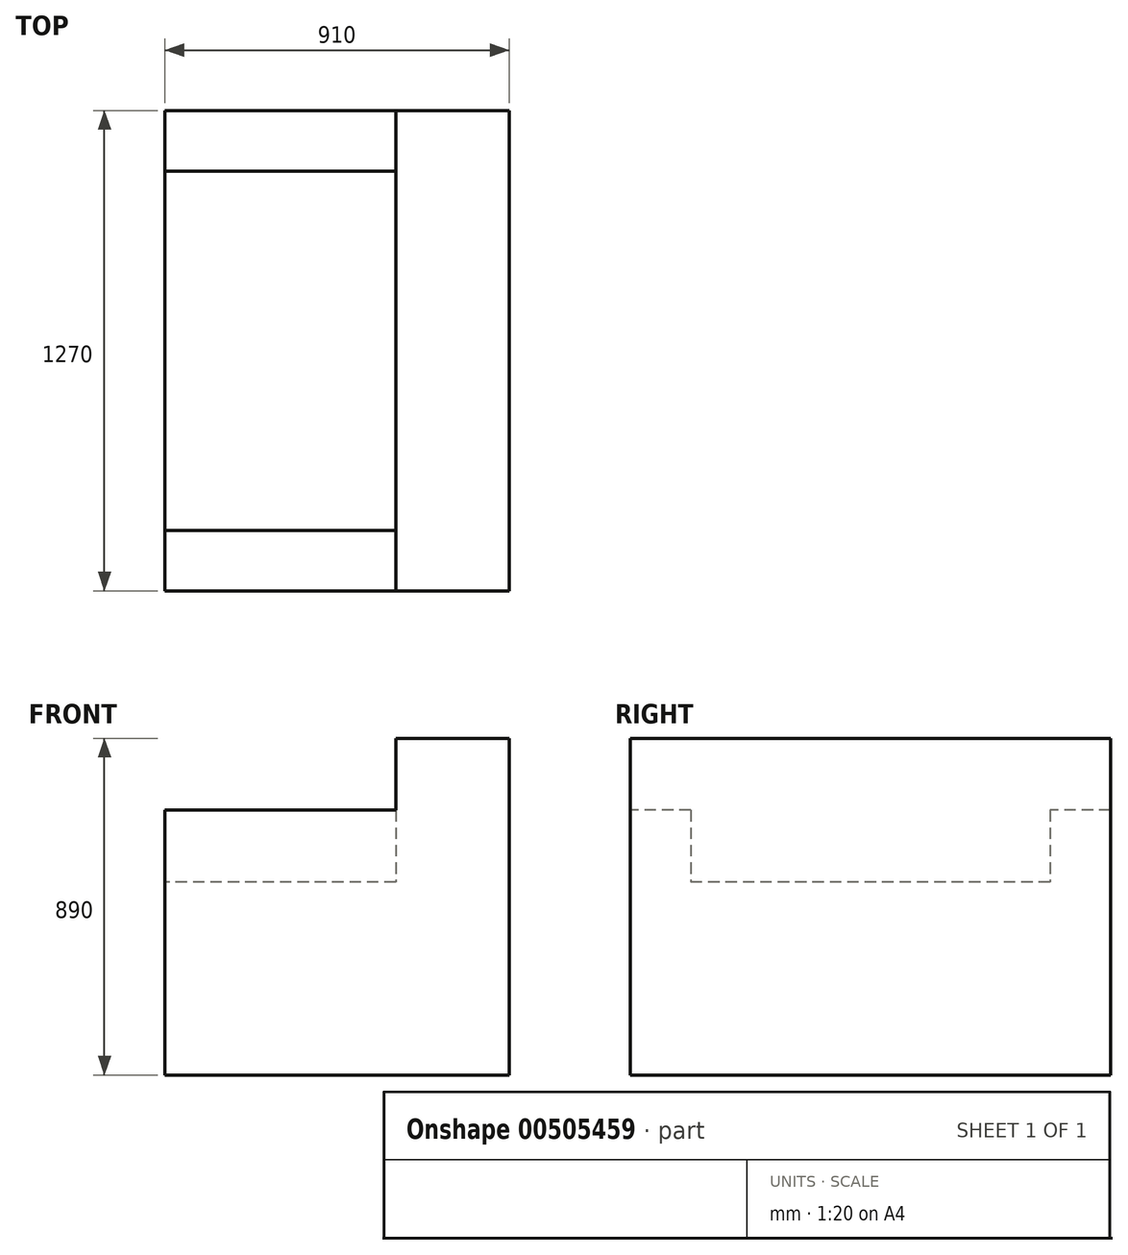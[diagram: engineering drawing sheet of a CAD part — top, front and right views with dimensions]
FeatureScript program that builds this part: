
annotation { "Feature Type Name" : "Feature", "Feature Type Description" : "" }
export const myFeature = defineFeature(function(context is Context, id is Id, definition is map)
    precondition{}
    {
        {
            var Q0;
            Q0=qCreatedBy(makeId("Top.planeOp"),FACE);
            var sketch = newSketch(context, id + "F0", { "sketchPlane" : qUnion([Q0])});
            skLineSegment(sketch, "E0.bottom", {"start": v(465.5, 635) * mm, "end": v(-444.5, 635) * mm});
            skLineSegment(sketch, "E0.top", {"start": v(465.5, -635) * mm, "end": v(-444.5, -635) * mm});
            skLineSegment(sketch, "E0.left", {"start": v(465.5, 635) * mm, "end": v(465.5, -635) * mm});
            skLineSegment(sketch, "E0.right", {"start": v(-444.5, 635) * mm, "end": v(-444.5, -635) * mm});
            skPoint(sketch, "E0.middle", {"position": v(10.5, 0) * mm});
            skSolve(sketch);
        }
        {
            var Q0;
            Q0 = qSketchRegion(id + "F0", true);
            extrude(context, id + "F1", {"entities" : qUnion([Q0]), "depth" : 890 * mm});
        }
        {
            var Q0;
            Q0=makeQuery(id+"F1.opExtrude","SWEPT_FACE",FACE,{"disambiguationData":[OSD([sQuery(id+"F0.wireOp",EDGE,"E0.right")])]});
            var sketch = newSketch(context, id + "F2", { "sketchPlane" : qUnion([Q0])});
            skLineSegment(sketch, "E1.bottom", {"start": v(-475, 890) * mm, "end": v(475, 890) * mm});
            skLineSegment(sketch, "E1.top", {"start": v(-475, 510) * mm, "end": v(475, 510) * mm});
            skLineSegment(sketch, "E1.left", {"start": v(-475, 890) * mm, "end": v(-475, 510) * mm});
            skLineSegment(sketch, "E1.right", {"start": v(475, 890) * mm, "end": v(475, 510) * mm});
            skLineSegment(sketch, "E2", {"start": v(0, 890) * mm, "end": v(0, 510) * mm, "construction": true});
            skSolve(sketch);
        }
        {
            var Q0;
            Q0 = qSketchRegion(id + "F2", true);
            extrude(context, id + "F3", {"entities" : qUnion([Q0]), "operationType" : NewBodyOperationType.REMOVE, "oppositeDirection" : true, "depth" : 610 * mm});
        }
        {
            var Q0;
            Q0=makeQuery(id+"F1.opExtrude","SWEPT_FACE",FACE,{"disambiguationData":[OSD([sQuery(id+"F0.wireOp",EDGE,"E0.right")])]});
            var sketch = newSketch(context, id + "F4", { "sketchPlane" : qUnion([Q0])});
            skLineSegment(sketch, "E3.bottom", {"start": v(-635, 890) * mm, "end": v(-475, 890) * mm});
            skLineSegment(sketch, "E3.top", {"start": v(-635, 700) * mm, "end": v(-475, 700) * mm});
            skLineSegment(sketch, "E3.left", {"start": v(-635, 890) * mm, "end": v(-635, 700) * mm});
            skLineSegment(sketch, "E3.right", {"start": v(-475, 890) * mm, "end": v(-475, 700) * mm});
            skLineSegment(sketch, "E4.bottom", {"start": v(475, 890) * mm, "end": v(635, 890) * mm});
            skLineSegment(sketch, "E4.top", {"start": v(475, 700) * mm, "end": v(635, 700) * mm});
            skLineSegment(sketch, "E4.left", {"start": v(475, 890) * mm, "end": v(475, 700) * mm});
            skLineSegment(sketch, "E4.right", {"start": v(635, 890) * mm, "end": v(635, 700) * mm});
            skSolve(sketch);
        }
        {
            var Q0;
            Q0 = qSketchRegion(id + "F4", true);
            var Q1;
            Q1=makeQuery(id+"F3.boolean.opBoolean","COPY",FACE,{"derivedFrom":makeQuery(id+"F3.opExtrude","CAP_FACE",FACE,{"disambiguationData":[OSD([sQuery(id+"F2.wireOp",EDGE,"E1.bottom"),sQuery(id+"F2.wireOp",EDGE,"E1.top"),sQuery(id+"F2.wireOp",EDGE,"E1.left"),sQuery(id+"F2.wireOp",EDGE,"E1.right")])],"isStart":false})});
            extrude(context, id + "F5", {"entities" : qUnion([Q0]), "operationType" : NewBodyOperationType.REMOVE, "endBound" : BoundingType.UP_TO_SURFACE, "oppositeDirection" : true, "endBoundEntityFace" : qUnion([Q1]), "depth" : 420 * mm});
        }
    });
